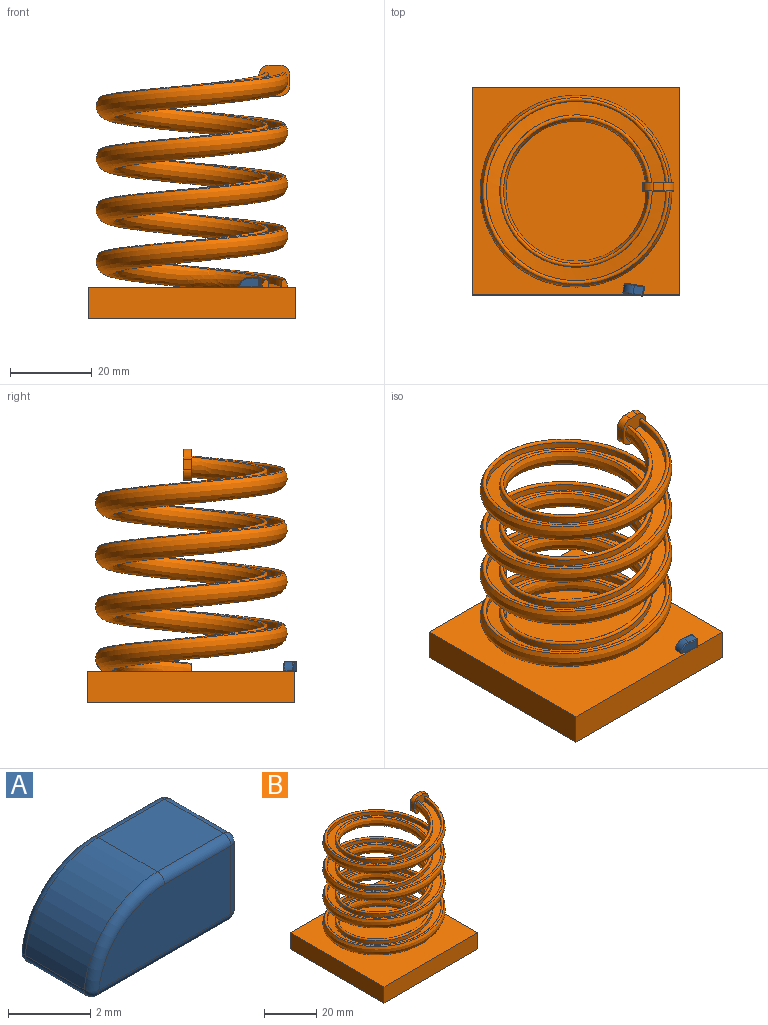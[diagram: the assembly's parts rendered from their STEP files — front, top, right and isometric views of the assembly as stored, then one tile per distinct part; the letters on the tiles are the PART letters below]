
ASSEMBLY  parts=2 mates=1
PART A: 23 faces, bbox 5.3x2.5x2.7 mm
  f0: plane 4.56x2.03mm, normal (0,0,-1), area 9.3mm2, adj f7,f11,f15,f16
  f1: plane 2.03x2.03mm, normal (1,0,0), area 4.1mm2, adj f10,f11,f17,f18
  f2: plane 2.29x2.03mm, normal (0,0,1), area 4.6mm2, adj f5,f9,f17,f22
  f3: plane 4.56x2.03mm, normal (0,-1,0), area 8.2mm2, adj f15,f18,f21,f22
  f4: plane 4.56x2.03mm, normal (0,1,0), area 8.2mm2, adj f7,f8,f9,f10
  f5: cylinder r=2.54mm len=2.52mm, axis (0,-1,0), area 7.5mm2, adj f2,f8,f16,f21
  f6: sphere r=0.25mm, area 0.1mm2, adj f7,f10,f11
  f7: cylinder r=0.25mm len=4.56mm, axis (1,0,0), area 1.8mm2, adj f0,f4,f6,f12
  f8: torus R=2.29mm, axis (0,-1,0), area 1.4mm2, adj f4,f5,f9,f12
  f9: cylinder r=0.25mm len=2.29mm, axis (-1,0,0), area 0.9mm2, adj f2,f4,f8,f13
  f10: cylinder r=0.25mm len=2.03mm, axis (0,0,1), area 0.8mm2, adj f1,f4,f6,f13
  f11: cylinder r=0.25mm len=2.03mm, axis (0,-1,0), area 0.8mm2, adj f0,f1,f6,f14
  f12: sphere r=0.25mm, area 0.1mm2, adj f7,f8,f16
  f13: sphere r=0.25mm, area 0.1mm2, adj f9,f10,f17
  f14: sphere r=0.25mm, area 0.1mm2, adj f11,f15,f18
  f15: cylinder r=0.25mm len=4.56mm, axis (-1,0,0), area 1.8mm2, adj f0,f3,f14,f19
  f16: cylinder r=0.25mm len=2.03mm, axis (0,-1,0), area 0.9mm2, adj f0,f5,f12,f19
  f17: cylinder r=0.25mm len=2.03mm, axis (0,1,0), area 0.8mm2, adj f1,f2,f13,f20
  f18: cylinder r=0.25mm len=2.03mm, axis (0,0,-1), area 0.8mm2, adj f1,f3,f14,f20
  f19: sphere r=0.25mm, area 0.1mm2, adj f15,f16,f21
  f20: sphere r=0.25mm, area 0.1mm2, adj f17,f18,f22
  f21: torus R=2.29mm, axis (0,-1,0), area 1.4mm2, adj f3,f5,f19,f22
  f22: cylinder r=0.25mm len=2.29mm, axis (1,0,0), area 0.9mm2, adj f2,f3,f20,f21
PART B: 24 faces, bbox 51.4x51.4x62.8 mm
  f0: plane 2.17x1.62mm, normal (0,-1,0), area 2.6mm2, adj f4,f5,f6,f23
  f1: plane 2.17x1.62mm, normal (0,-1,0), area 2.6mm2, adj f2,f5,f7,f23
  f2: cylinder r=18.67mm len=52.36mm, axis (0,0,1), area 746.3mm2, adj f1,f3,f7,f13
  f3: bspline ~50.8x43.94mm, area 1695.3mm2, adj f2,f4,f13,f23
  f4: cylinder r=21.97mm len=52.36mm, axis (0,0,1), area 886.6mm2, adj f0,f3,f6,f13
  f5: bspline ~56.69x50.72mm, area 6943.2mm2, adj f0,f1,f6,f7,f13,f23
  f6: bspline ~52.4x45.8mm, area 719.9mm2, adj f0,f4,f5,f13
  f7: bspline ~52.41x37.35mm, area 590mm2, adj f1,f2,f5,f13
  f8: plane 2.54x2.03mm, normal (1,0,0), area 5.2mm2, adj f12,f13,f14,f17
  f9: plane 2.54x2.03mm, normal (0,0,-1), area 5.2mm2, adj f12,f13,f14,f15
  f10: plane 2.54x2.03mm, normal (-1,0,0), area 5.2mm2, adj f12,f13,f15,f16
  f11: plane 2.54x2.03mm, normal (0,0,1), area 5.2mm2, adj f12,f13,f16,f17
  f12: plane 7.62x7.62mm, normal (0,1,0), area 52.5mm2, adj f8,f9,f10,f11,f14,f15,f16,f17
  f13: plane 8.24x8.24mm, normal (0,-1,0), area 31.5mm2, adj f2,f3,f4,f5,f6,f7,f8,f9
  f14: cylinder r=2.54mm len=2.54mm, axis (0,1,0), area 8.1mm2, adj f8,f9,f12,f13
  f15: cylinder r=2.54mm len=2.54mm, axis (0,-1,0), area 8.1mm2, adj f9,f10,f12,f13
  f16: cylinder r=2.54mm len=2.54mm, axis (0,1,0), area 8.1mm2, adj f10,f11,f12,f13
  f17: cylinder r=2.54mm len=2.54mm, axis (0,-1,0), area 8.1mm2, adj f8,f11,f12,f13
  f18: plane 50.8x7.62mm, normal (-1,0,0), area 387.1mm2, adj f19,f21,f22,f23
  f19: plane 50.8x7.62mm, normal (0,-1,0), area 387.1mm2, adj f18,f20,f22,f23
  f20: plane 50.8x7.62mm, normal (1,0,0), area 387.1mm2, adj f19,f21,f22,f23
  f21: plane 50.8x7.62mm, normal (0,1,0), area 387.1mm2, adj f18,f20,f22,f23
  f22: plane 50.8x50.8mm, normal (0,0,-1), area 2580.6mm2, adj f18,f19,f20,f21
  f23: plane 50.8x50.8mm, normal (0,0,1), area 2415.2mm2, adj f0,f1,f3,f5,f18,f19,f20,f21
PLACE A rot(axis=(0,0,-1),9.1deg) t=(14.35,-22.84,1.27)mm
PLACE B at identity fixed
MATE pin_slot B.f23 <-> A.f0  axis (0,0,1) through (20.32,0,0)mm
